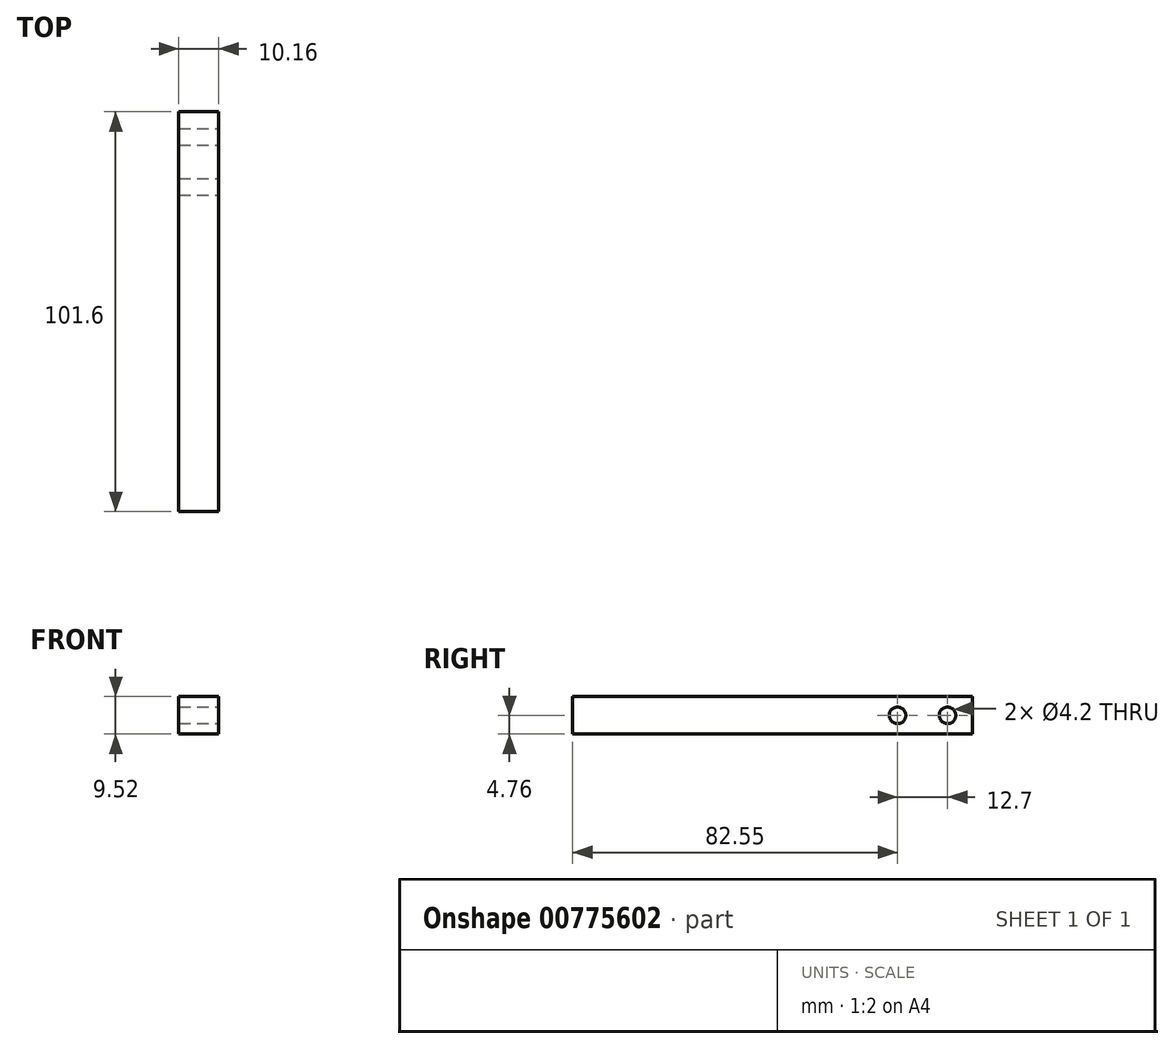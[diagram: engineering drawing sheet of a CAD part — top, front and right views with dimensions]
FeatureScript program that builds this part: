
annotation { "Feature Type Name" : "Feature", "Feature Type Description" : "" }
export const myFeature = defineFeature(function(context is Context, id is Id, definition is map)
    precondition{}
    {
        {
            var Q0;
            Q0=qCreatedBy(makeId("Right.planeOp"),FACE);
            var sketch = newSketch(context, id + "F0", { "sketchPlane" : qUnion([Q0])});
            skLineSegment(sketch, "E0.bottom", {"start": v(50.8, -4.76) * mm, "end": v(-50.8, -4.76) * mm});
            skLineSegment(sketch, "E0.top", {"start": v(50.8, 4.76) * mm, "end": v(-50.8, 4.76) * mm});
            skLineSegment(sketch, "E0.left", {"start": v(50.8, -4.76) * mm, "end": v(50.8, 4.76) * mm});
            skLineSegment(sketch, "E0.right", {"start": v(-50.8, -4.76) * mm, "end": v(-50.8, 4.76) * mm});
            skPoint(sketch, "E0.middle", {"position": v(0, 0) * mm});
            skSolve(sketch);
        }
        {
            var Q0;
            Q0 = qSketchRegion(id + "F0", true);
            extrude(context, id + "F1", {"entities" : qUnion([Q0]), "depth" : 10.16 * mm, "offsetDistance" : 25.4 * mm});
        }
        {
            var Q0;
            Q0=makeQuery(id+"F1.opExtrude","CAP_FACE",FACE,{"disambiguationData":[OSD([sQuery(id+"F0.wireOp",EDGE,"E0.bottom"),sQuery(id+"F0.wireOp",EDGE,"E0.top"),sQuery(id+"F0.wireOp",EDGE,"E0.left"),sQuery(id+"F0.wireOp",EDGE,"E0.right")])],"isStart":false});
            var sketch = newSketch(context, id + "F2", { "sketchPlane" : qUnion([Q0])});
            skLineSegment(sketch, "E1", {"start": v(50.8, 0) * mm, "end": v(-50.8, 0) * mm});
            skCircle(sketch, "E2", {"center": v(44.45, 0) * mm, "radius": 2.1 * mm});
            skCircle(sketch, "E3", {"center": v(31.75, 0) * mm, "radius": 2.1 * mm});
            skSolve(sketch);
        }
        {
            var Q0;
            Q0 = qSketchRegion(id + "F2", true);
            extrude(context, id + "F3", {"entities" : qUnion([Q0]), "operationType" : NewBodyOperationType.REMOVE, "endBound" : BoundingType.THROUGH_ALL, "oppositeDirection" : true, "depth" : 25.4 * mm, "offsetDistance" : 25.4 * mm});
        }
    });
